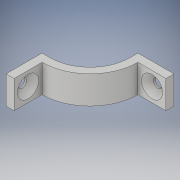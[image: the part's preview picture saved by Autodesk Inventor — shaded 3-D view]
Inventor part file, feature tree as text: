
AUTODESK INVENTOR PART (.ipt)
format: ipt  version: 2019 (Build 230136000, 136)  size: 142,848 bytes
history: native  units: mm
features: extrude x3, sketch x3, chamfer x2, projected_geometry x1
ambient origin geometry x8: Origin, YZ Plane, XZ Plane, XY Plane, X Axis, Y Axis, Z Axis, Center Point
bodies: Body1 (feature_tree), Body2 (feature_tree)
feature tree (9):
  extrude  "Extrusion2"  Depth=12.0mm
  extrude  "Extrusion3"  Depth=9.0mm
  chamfer  "Chamfer1"  Distance=2.0mm
  extrude  "Extrusion4"  Depth=7.0mm TaperAngle=0.0deg
  chamfer  "Chamfer2"  Distance=2.3mm
  sketch  "Sketch3"  dims[d10=10.0mm d11=12.0mm]
  sketch  "Sketch4"  dims[d12=2.0mm d13=9.0mm]
  projected_geometry  "Projected Loop1"
  sketch  "Sketch6"  dims[d14=9.0mm d15=2.0mm d16=7.0mm d17=0.0mm d18=2.3mm d19=2.0mm d20=0.0mm d21=1.5mm d22=2.0mm d23=45.0deg d24=2.3mm d25=2.0mm d26=0.0mm d27=1.5mm d28=2.0mm d29=45.0deg]
